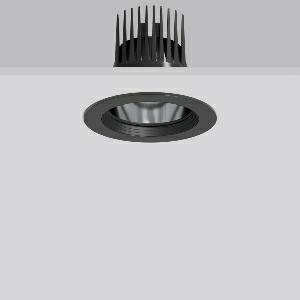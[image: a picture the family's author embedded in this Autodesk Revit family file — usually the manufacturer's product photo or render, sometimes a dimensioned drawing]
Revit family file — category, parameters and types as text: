
# Revit family: heledon_maxi_e_901764_003_3_0c83
name_source: partatom
category: Lighting Fixtures
units: mm (PartAtom-declared; Revit-internal decimal feet)

## family parameters
Cut with Voids When Loaded = No
Host = Face
Light Source = No
Part Type = Normal
Room Calculation Point = No
Round Connector Dimension = Use Diameter
Shared = No

## types (1)
- HELEDON maxi E (1 x LED Modul 935, 4350 lm, 3500)
    Apparent Load = 35 VA
    Approval mark = CE
    CIE Flux Codes = 100 100 100 100 100
    Color Rendering = 92
    Color Temperature = 3500
    Default Elevation = 1800 mm
    Description = Series: HELEDON maxi
Round recessed downlight. Housing: die-cast aluminium, powder-coated. Black plastic ring and recessed LED to prevent glare from the side. Optical assembly with reflector made of MIRO-Silver with 98% total light reflection for outstanding efficiency - can be changed without tools. Best colour rendering index Ra>90. Suitable for Recessed ceiling mounting. Installation without tools thanks to spring fastening system. Including separate LED converter with connecting cable 600 mm.High quality converter without flickering and stroboscopic effect. Through-wiring box (5 pole) available as accessory. The following accessories can be mounted without use of tools: interchangeable lenses, decorative glasses, honeycomb louvre, clear and frosted diffusers, white interchangeable plastic ring. 
Colour: deep black, matt (RAL 9005)
Diameter: 162 mm
Height: 3 mm
Cut-out diameter: 152 mm
Recess height: 200 mm
Luminaire: recess height: 135 mm
Lamp: LED
Socket: without socket
Colour temperature: 3500K
Colour rendering index (CRI): 92
System power: 35 W
Rated luminous flux: 4350 lm
Luminous efficiency: 124 lm/W
Control gear: Regulated power supply
Protection class: II
Type of protection: IP 20
    Height = 0 mm  [stored 0 ft]
    Lamp = 1 x LED Modul 935
    Lamp Light Flux = 4350 lm
    Lamp count = 1
    Length = 162 mm
    Lifetime = 50000 h
    Luminous efficacy = 124 lm/W
    Manufacturer = RZB
    ModVariant = No
    Model = 901764.003.3
    Mounting Place = Ceiling
    Mounting Type = Recessed
    Number of Poles = 1
    OnlyDefault = Yes
    Power Factor = 1
    Product Name = HELEDON maxi E
    Product group = Recessed downlights
    ProductGroupID = 402
    Protection Class = Protection class II
    Protection Degree = IP 20
    RLX_Detail_Level = 1
    RLX_Emergency_Light_Flux = 0 lm
    RLX_Emergency_Type = 0
    RLX_Emergency_Type_DB = No
    RlxData = <blob elided: 121197 chars, md5=818df730>
    Socket = socket
    Standby Power = 0 W
    System Light Flux = 4350 lm
    System Power = 35 W
    Type Comments = Product without accessories
    Type Image = 901662.003.jpg
    URL = http://relux.com
    VarID = ---
    Voltage = 230 V
    Voltage Range = 220-240 V
    Weight = 0.00 kg
    Width = 0 mm  [stored 0 ft]

note: [stored X ft] marks values corroborated as IEEE doubles in the binary element streams (Revit-internal decimal feet)

## geometry (parser evidence)
native form markers: Blend x4, Sweep x10
no freeform markers — native parametric forms only
